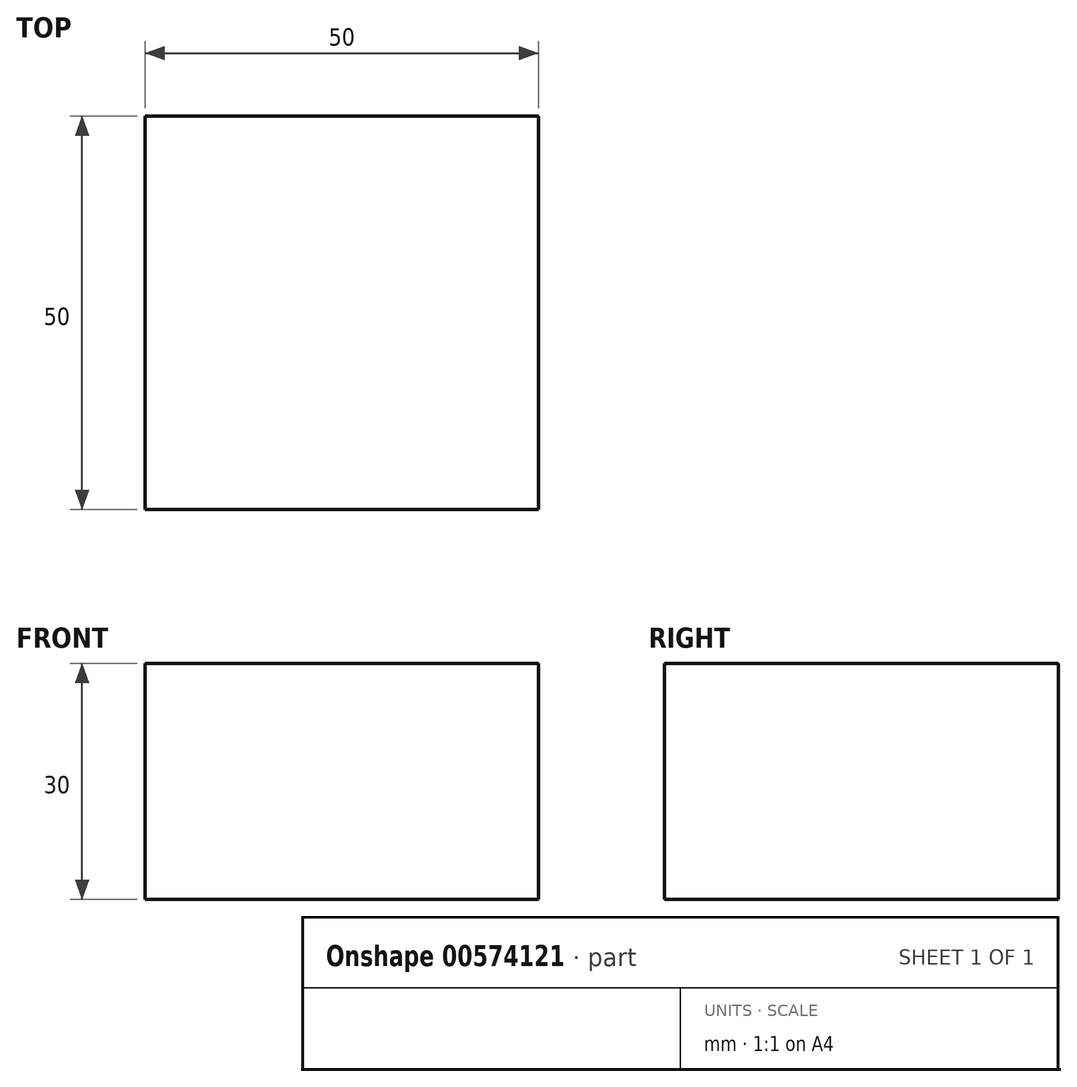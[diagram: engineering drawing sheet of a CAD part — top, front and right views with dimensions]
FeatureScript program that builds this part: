
annotation { "Feature Type Name" : "Feature", "Feature Type Description" : "" }
export const myFeature = defineFeature(function(context is Context, id is Id, definition is map)
    precondition{}
    {
        {
            var Q0;
            Q0=qCreatedBy(makeId("Top.planeOp"),FACE);
            var sketch = newSketch(context, id + "F0", { "sketchPlane" : qUnion([Q0])});
            skLineSegment(sketch, "E0.bottom", {"start": v(-25, 25) * mm, "end": v(25, 25) * mm});
            skLineSegment(sketch, "E0.top", {"start": v(-25, -25) * mm, "end": v(25, -25) * mm});
            skLineSegment(sketch, "E0.left", {"start": v(-25, 25) * mm, "end": v(-25, -25) * mm});
            skLineSegment(sketch, "E0.right", {"start": v(25, 25) * mm, "end": v(25, -25) * mm});
            skPoint(sketch, "E0.middle", {"position": v(0, 0) * mm});
            skSolve(sketch);
        }
        {
            var Q0;
            Q0=makeQuery(id+"F0.imprint","IMPRINT",FACE,{"disambiguationData":[TD([[makeQuery(id+"F0.imprint","IMPRINT",EDGE,{"derivedFrom":sQuery(id+"F0.wireOp",EDGE,"E0.bottom")}),-1.0]])]});
            extrude(context, id + "F1", {"entities" : qUnion([Q0]), "depth" : 30 * mm, "offsetDistance" : 25 * mm});
        }
    });
